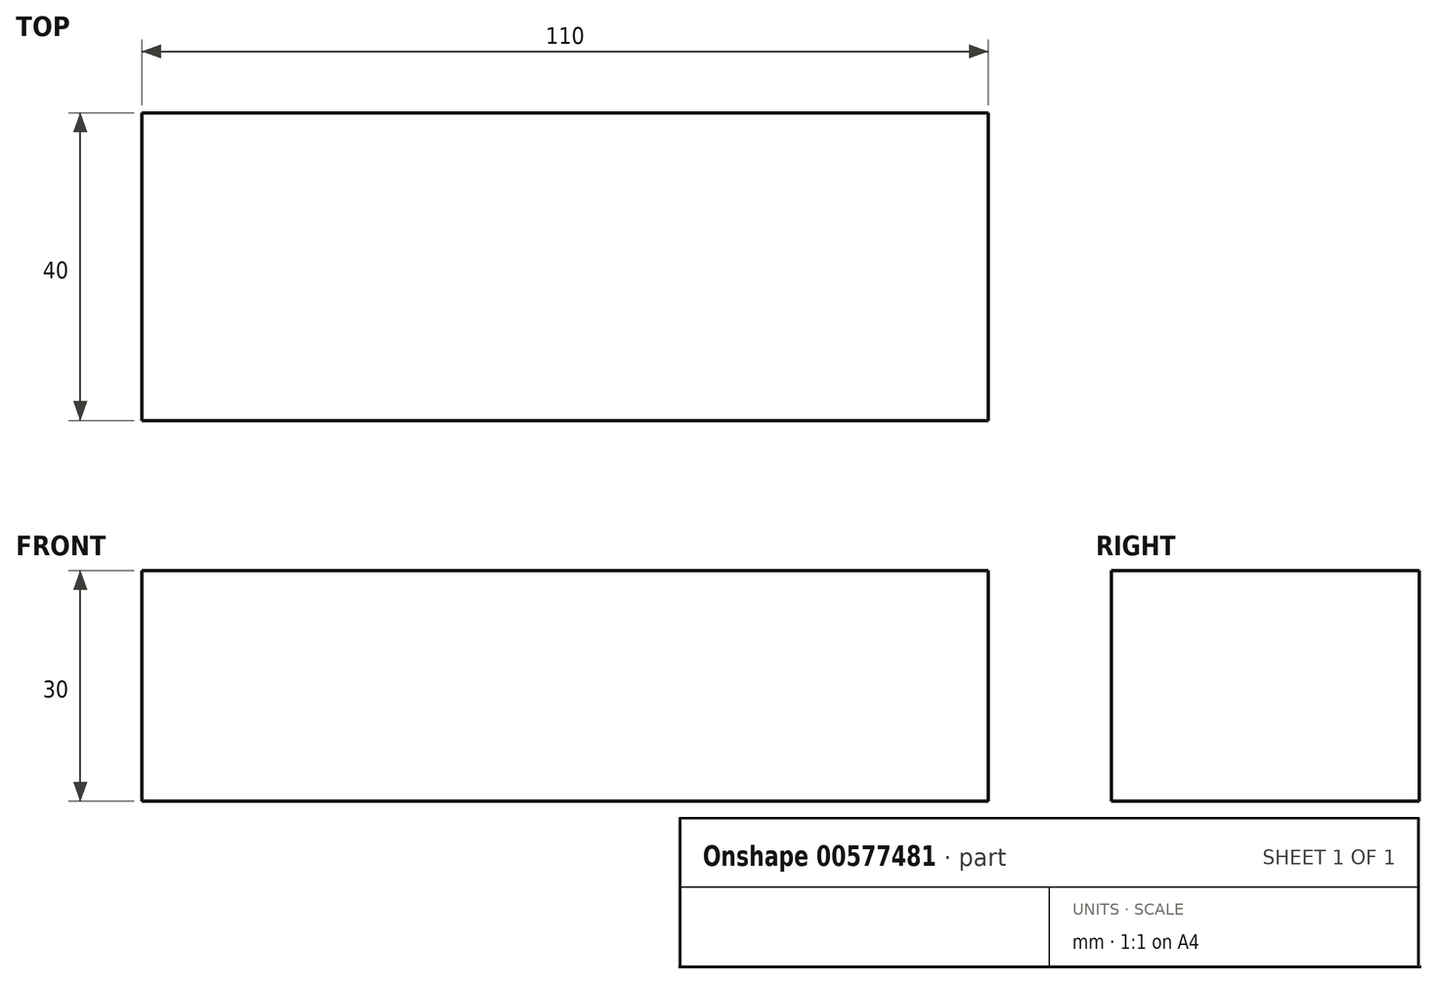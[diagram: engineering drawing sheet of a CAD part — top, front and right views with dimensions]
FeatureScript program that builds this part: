
annotation { "Feature Type Name" : "Feature", "Feature Type Description" : "" }
export const myFeature = defineFeature(function(context is Context, id is Id, definition is map)
    precondition{}
    {
        {
            var Q0;
            Q0=qCreatedBy(makeId("Top.planeOp"),FACE);
            var sketch = newSketch(context, id + "F0", { "sketchPlane" : qUnion([Q0])});
            skLineSegment(sketch, "E0.bottom", {"start": v(-33.94, -42.75) * mm, "end": v(-143.94, -42.75) * mm});
            skLineSegment(sketch, "E0.top", {"start": v(-33.94, -2.75) * mm, "end": v(-143.94, -2.75) * mm});
            skLineSegment(sketch, "E0.left", {"start": v(-33.94, -42.75) * mm, "end": v(-33.94, -2.75) * mm});
            skLineSegment(sketch, "E0.right", {"start": v(-143.94, -42.75) * mm, "end": v(-143.94, -2.75) * mm});
            skPoint(sketch, "E0.middle", {"position": v(-88.94, -22.75) * mm});
            skSolve(sketch);
        }
        {
            var Q0;
            Q0=qSketchRegion(id+"F0",true);
            extrude(context, id + "F1", {"entities" : qUnion([Q0]), "depth" : 30 * mm});
        }
    });
